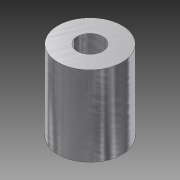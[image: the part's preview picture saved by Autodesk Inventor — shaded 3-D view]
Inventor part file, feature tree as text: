
AUTODESK INVENTOR PART (.ipt)
format: ipt  version: 2014 (Build 180170000, 170)  size: 102,400 bytes
history: native  units: mm
features: extrude x2, sketch x2
ambient origin geometry x8: Origin, YZ Plane, XZ Plane, XY Plane, X Axis, Y Axis, Z Axis, Center Point
bodies: Solid1 (feature_tree)
feature tree (4):
  extrude  "Extrusion1"  Depth=6.0mm
  extrude  "Extrusion2"  Depth=15.0mm
  sketch  "Sketch1"  dims[d0=20.0mm d1=6.0mm]
  sketch  "Sketch2"  dims[d2=25.0mm d3=0.0mm d4=8.0mm d5=15.0mm d6=0.0mm]
